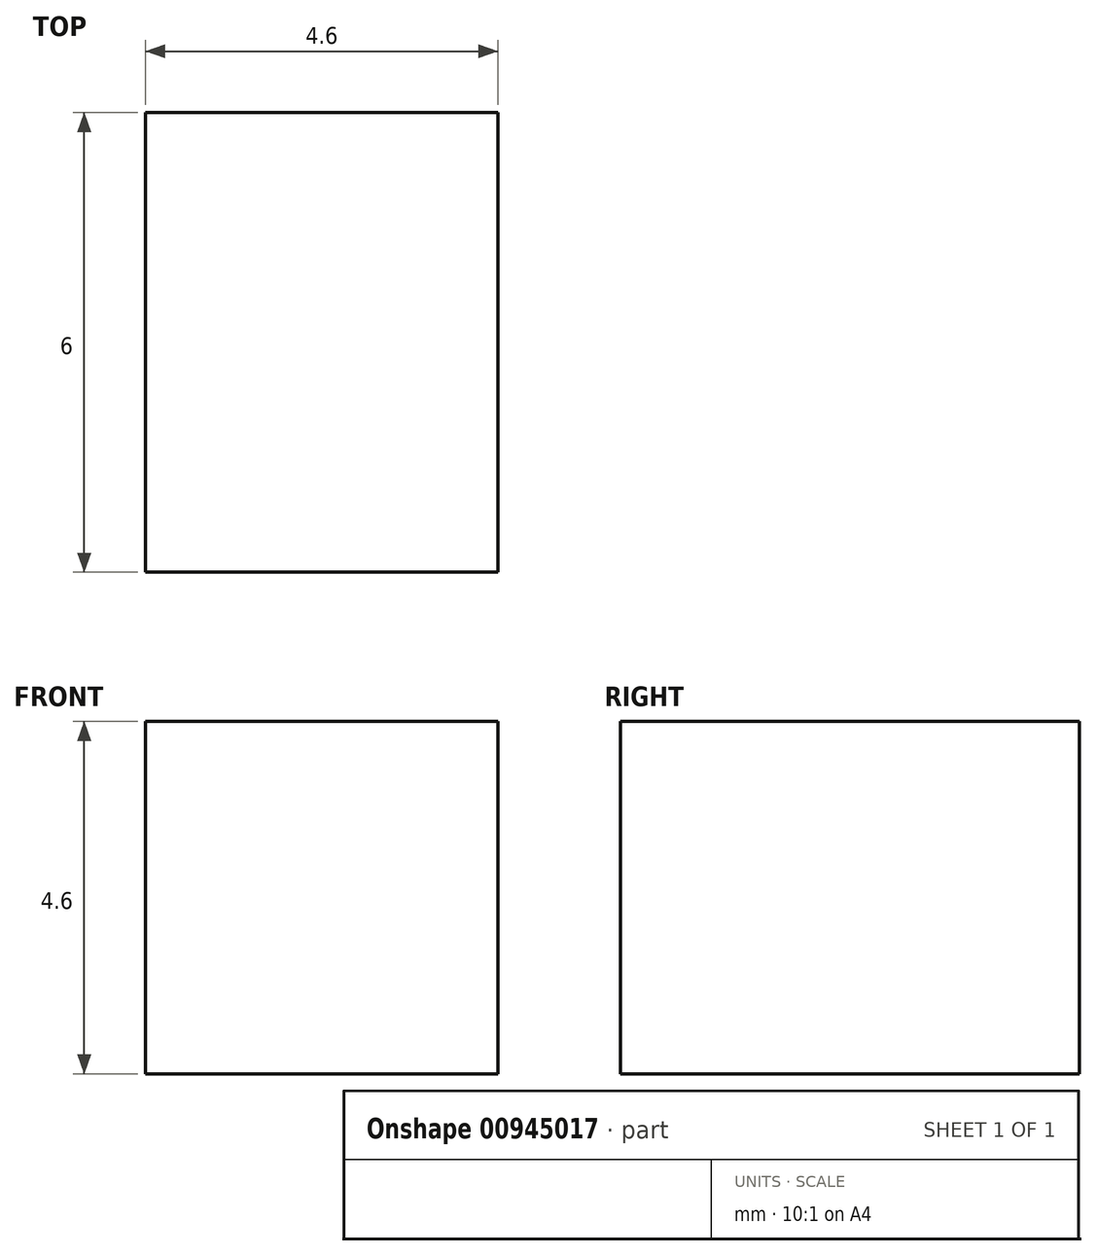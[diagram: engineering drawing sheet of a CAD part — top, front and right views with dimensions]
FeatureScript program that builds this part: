
annotation { "Feature Type Name" : "Feature", "Feature Type Description" : "" }
export const myFeature = defineFeature(function(context is Context, id is Id, definition is map)
    precondition{}
    {
        {
            var Q0;
            Q0=qCreatedBy(makeId("Front.planeOp"),FACE);
            var sketch = newSketch(context, id + "F0", { "sketchPlane" : qUnion([Q0])});
            skLineSegment(sketch, "E0.bottom", {"start": v(2.3, -2.3) * mm, "end": v(-2.3, -2.3) * mm});
            skLineSegment(sketch, "E0.top", {"start": v(2.3, 2.3) * mm, "end": v(-2.3, 2.3) * mm});
            skLineSegment(sketch, "E0.left", {"start": v(2.3, -2.3) * mm, "end": v(2.3, 2.3) * mm});
            skLineSegment(sketch, "E0.right", {"start": v(-2.3, -2.3) * mm, "end": v(-2.3, 2.3) * mm});
            skPoint(sketch, "E0.middle", {"position": v(0, 0) * mm});
            skSolve(sketch);
        }
        {
            var Q0;
            Q0 = qSketchRegion(id + "F0", true);
            extrude(context, id + "F1", {"entities" : qUnion([Q0]), "depth" : 6 * mm, "offsetDistance" : 25 * mm});
        }
    });
